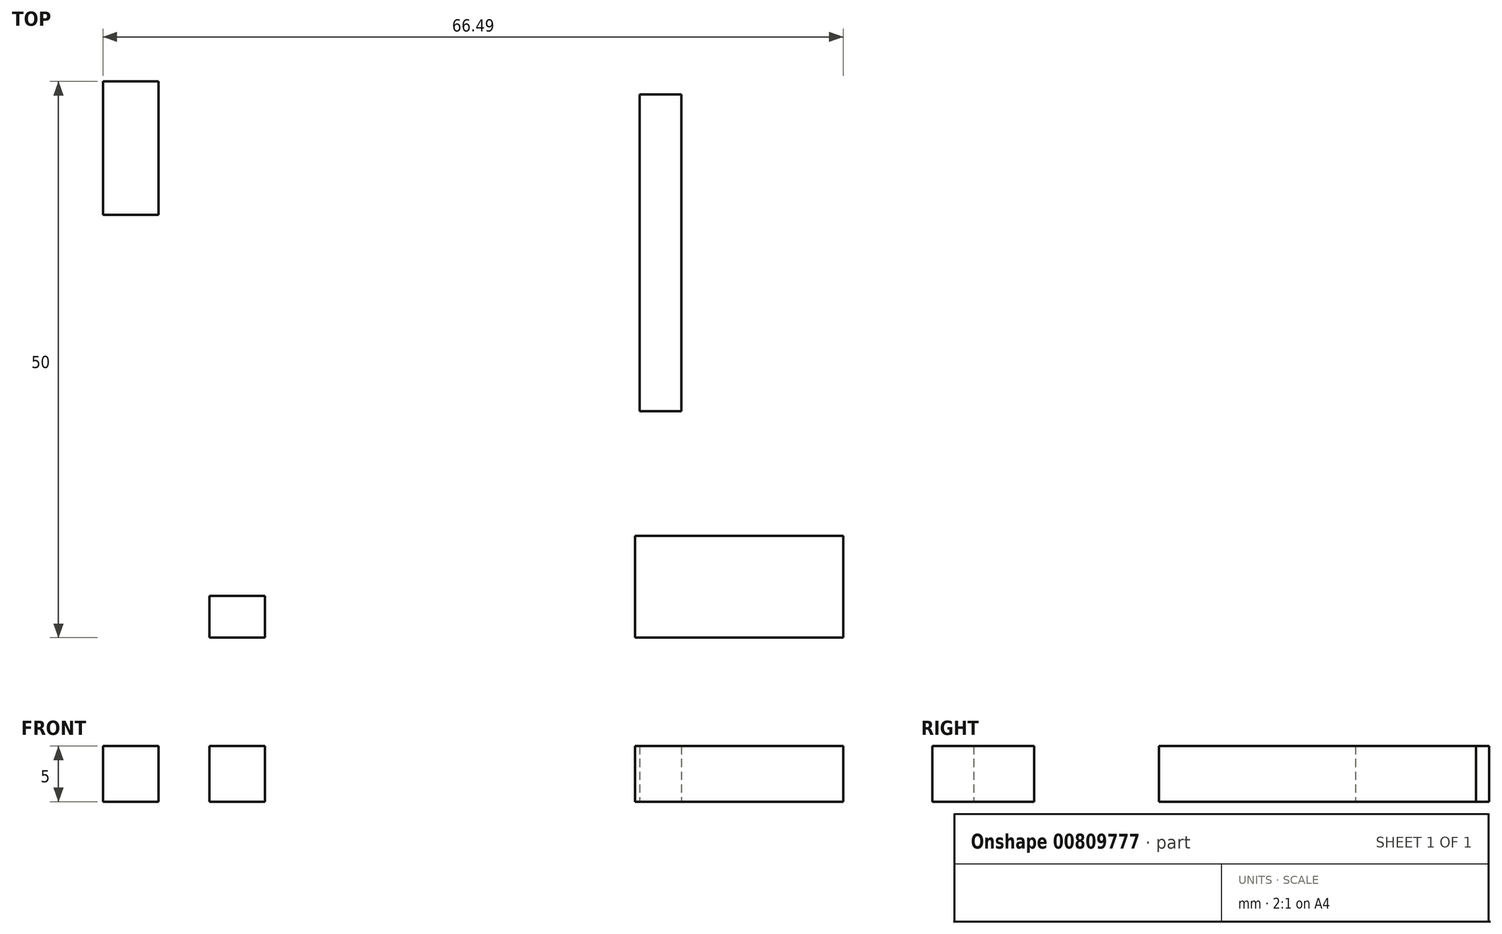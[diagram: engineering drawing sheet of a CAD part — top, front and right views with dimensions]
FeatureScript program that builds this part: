
annotation { "Feature Type Name" : "Feature", "Feature Type Description" : "" }
export const myFeature = defineFeature(function(context is Context, id is Id, definition is map)
    precondition{}
    {
        {
            var Q0;
            Q0=qCreatedBy(makeId("Top.planeOp"),FACE);
            var sketch = newSketch(context, id + "F0", { "sketchPlane" : qUnion([Q0])});
            skLineSegment(sketch, "E0.bottom", {"start": v(-41.87, 34.42) * mm, "end": v(-36.87, 34.42) * mm});
            skLineSegment(sketch, "E0.top", {"start": v(-41.87, 22.42) * mm, "end": v(-36.87, 22.42) * mm});
            skLineSegment(sketch, "E0.left", {"start": v(-41.87, 34.42) * mm, "end": v(-41.87, 22.42) * mm});
            skLineSegment(sketch, "E0.right", {"start": v(-36.87, 34.42) * mm, "end": v(-36.87, 22.42) * mm});
            skLineSegment(sketch, "E1.bottom", {"start": v(6.34, 33.24) * mm, "end": v(10.08, 33.24) * mm});
            skLineSegment(sketch, "E1.top", {"start": v(6.34, 4.78) * mm, "end": v(10.08, 4.78) * mm});
            skLineSegment(sketch, "E1.left", {"start": v(6.34, 33.24) * mm, "end": v(6.34, 4.78) * mm});
            skLineSegment(sketch, "E1.right", {"start": v(10.08, 33.24) * mm, "end": v(10.08, 4.78) * mm});
            skLineSegment(sketch, "E2.bottom", {"start": v(-32.3, -11.84) * mm, "end": v(-27.32, -11.84) * mm});
            skLineSegment(sketch, "E2.top", {"start": v(-32.3, -15.58) * mm, "end": v(-27.32, -15.58) * mm});
            skLineSegment(sketch, "E2.left", {"start": v(-32.3, -11.84) * mm, "end": v(-32.3, -15.58) * mm});
            skLineSegment(sketch, "E2.right", {"start": v(-27.32, -11.84) * mm, "end": v(-27.32, -15.58) * mm});
            skLineSegment(sketch, "E3.bottom", {"start": v(5.92, -6.44) * mm, "end": v(24.62, -6.44) * mm});
            skLineSegment(sketch, "E3.top", {"start": v(5.92, -15.58) * mm, "end": v(24.62, -15.58) * mm});
            skLineSegment(sketch, "E3.left", {"start": v(5.92, -6.44) * mm, "end": v(5.92, -15.58) * mm});
            skLineSegment(sketch, "E3.right", {"start": v(24.62, -6.44) * mm, "end": v(24.62, -15.58) * mm});
            skSolve(sketch);
        }
        {
            var Q0;
            Q0 = qSketchRegion(id + "F0", true);
            extrude(context, id + "F1", {"entities" : qUnion([Q0]), "depth" : 5 * mm, "offsetDistance" : 25 * mm});
        }
    });
